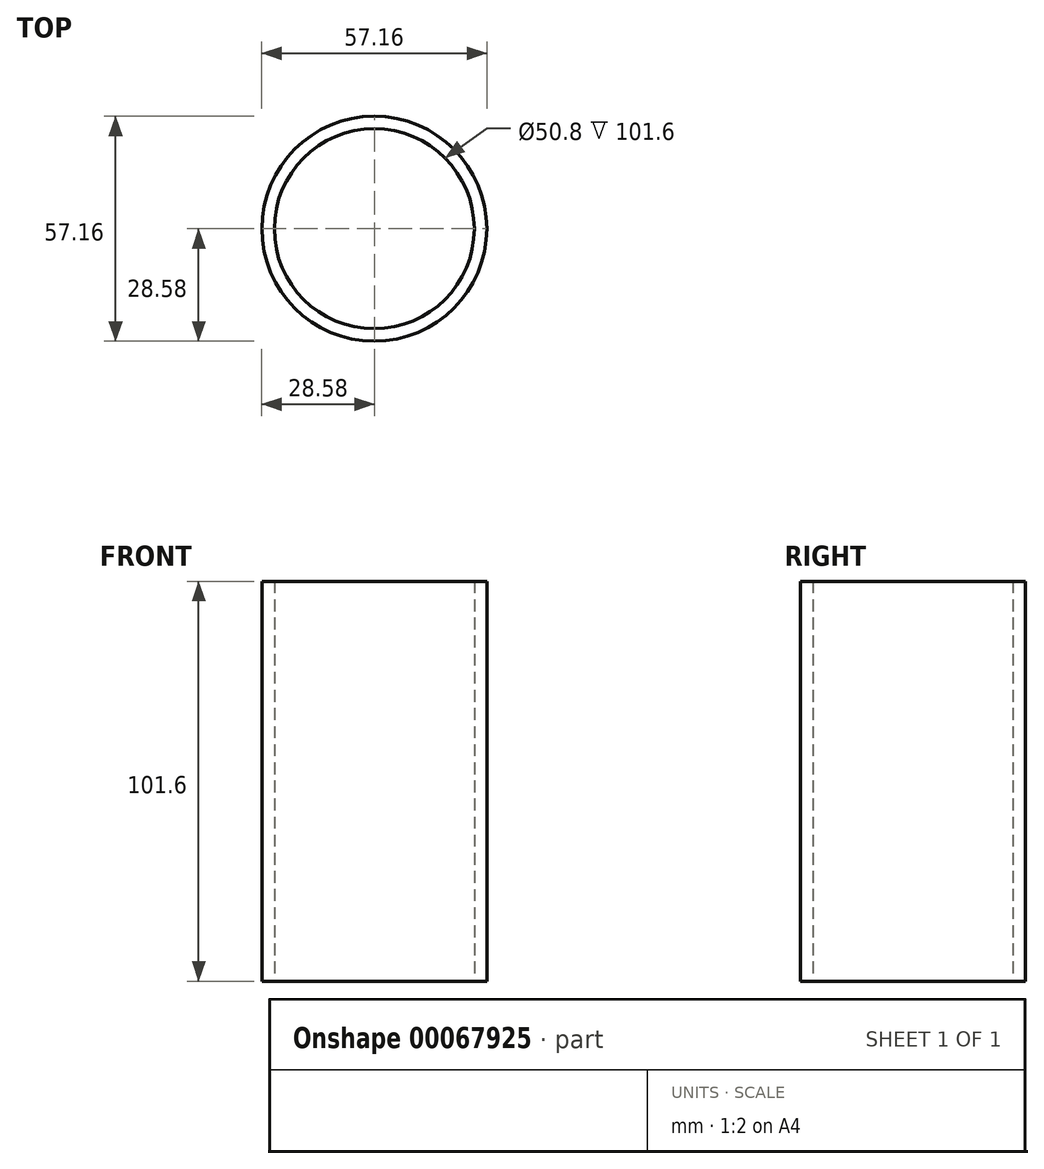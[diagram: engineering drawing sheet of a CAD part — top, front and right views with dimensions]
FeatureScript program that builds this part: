
annotation { "Feature Type Name" : "Feature", "Feature Type Description" : "" }
export const myFeature = defineFeature(function(context is Context, id is Id, definition is map)
    precondition{}
    {
        {
            var Q0;
            Q0=qCreatedBy(makeId("Top.planeOp"),FACE);
            var sketch = newSketch(context, id + "F0", { "sketchPlane" : qUnion([Q0])});
            skCircle(sketch, "E0", {"center": v(0, 0) * mm, "radius": 25.4 * mm});
            skCircle(sketch, "E1", {"center": v(0, 0) * mm, "radius": 28.58 * mm});
            skSolve(sketch);
        }
        {
            var Q0;
            Q0=makeQuery(id+"F0.imprint","IMPRINT",FACE,{"disambiguationData":[TD([[makeQuery(id+"F0.imprint","IMPRINT",EDGE,{"derivedFrom":sQuery(id+"F0.wireOp",EDGE,"E0")}),-1.0]])]});
            extrude(context, id + "F1", {"entities" : qUnion([Q0]), "depth" : 101.6 * mm});
        }
    });
